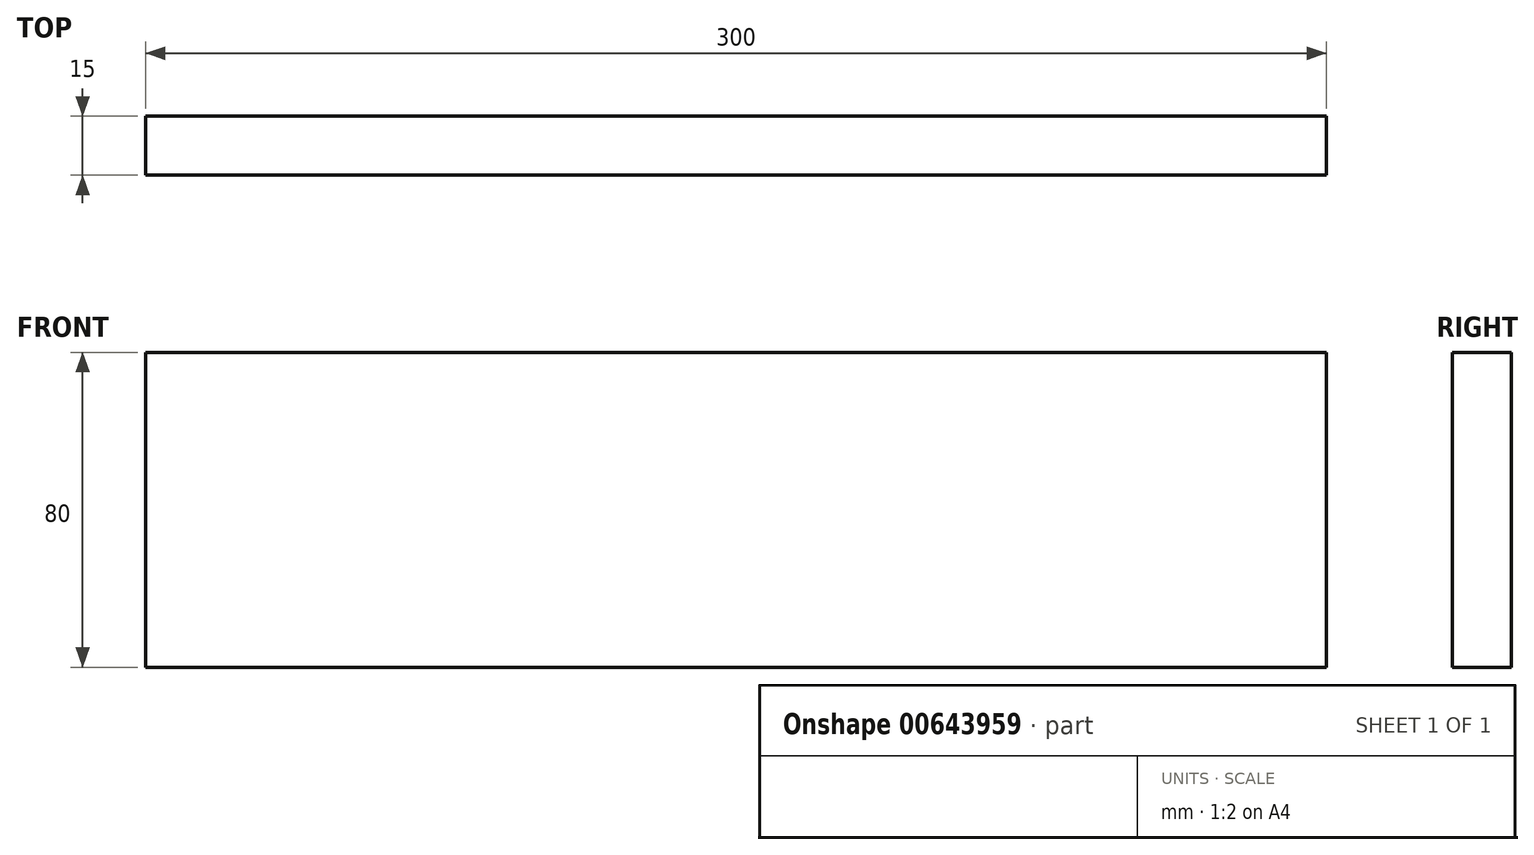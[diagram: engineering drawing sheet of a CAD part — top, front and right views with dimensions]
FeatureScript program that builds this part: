
annotation { "Feature Type Name" : "Feature", "Feature Type Description" : "" }
export const myFeature = defineFeature(function(context is Context, id is Id, definition is map)
    precondition{}
    {
        {
            var Q0;
            Q0=qCreatedBy(makeId("Front.planeOp"),FACE);
            var sketch = newSketch(context, id + "F0", { "sketchPlane" : qUnion([Q0])});
            skLineSegment(sketch, "E0.bottom", {"start": v(-150, 40) * mm, "end": v(150, 40) * mm});
            skLineSegment(sketch, "E0.top", {"start": v(-150, -40) * mm, "end": v(150, -40) * mm});
            skLineSegment(sketch, "E0.left", {"start": v(-150, 40) * mm, "end": v(-150, -40) * mm});
            skLineSegment(sketch, "E0.right", {"start": v(150, 40) * mm, "end": v(150, -40) * mm});
            skSolve(sketch);
        }
        {
            var Q0;
            Q0=makeQuery(id+"F0.imprint","IMPRINT",FACE,{"disambiguationData":[TD([[makeQuery(id+"F0.imprint","IMPRINT",EDGE,{"derivedFrom":sQuery(id+"F0.wireOp",EDGE,"E0.bottom")}),-1.0]])]});
            extrude(context, id + "F1", {"entities" : qUnion([Q0]), "depth" : 15 * mm, "offsetDistance" : 25 * mm});
        }
    });
